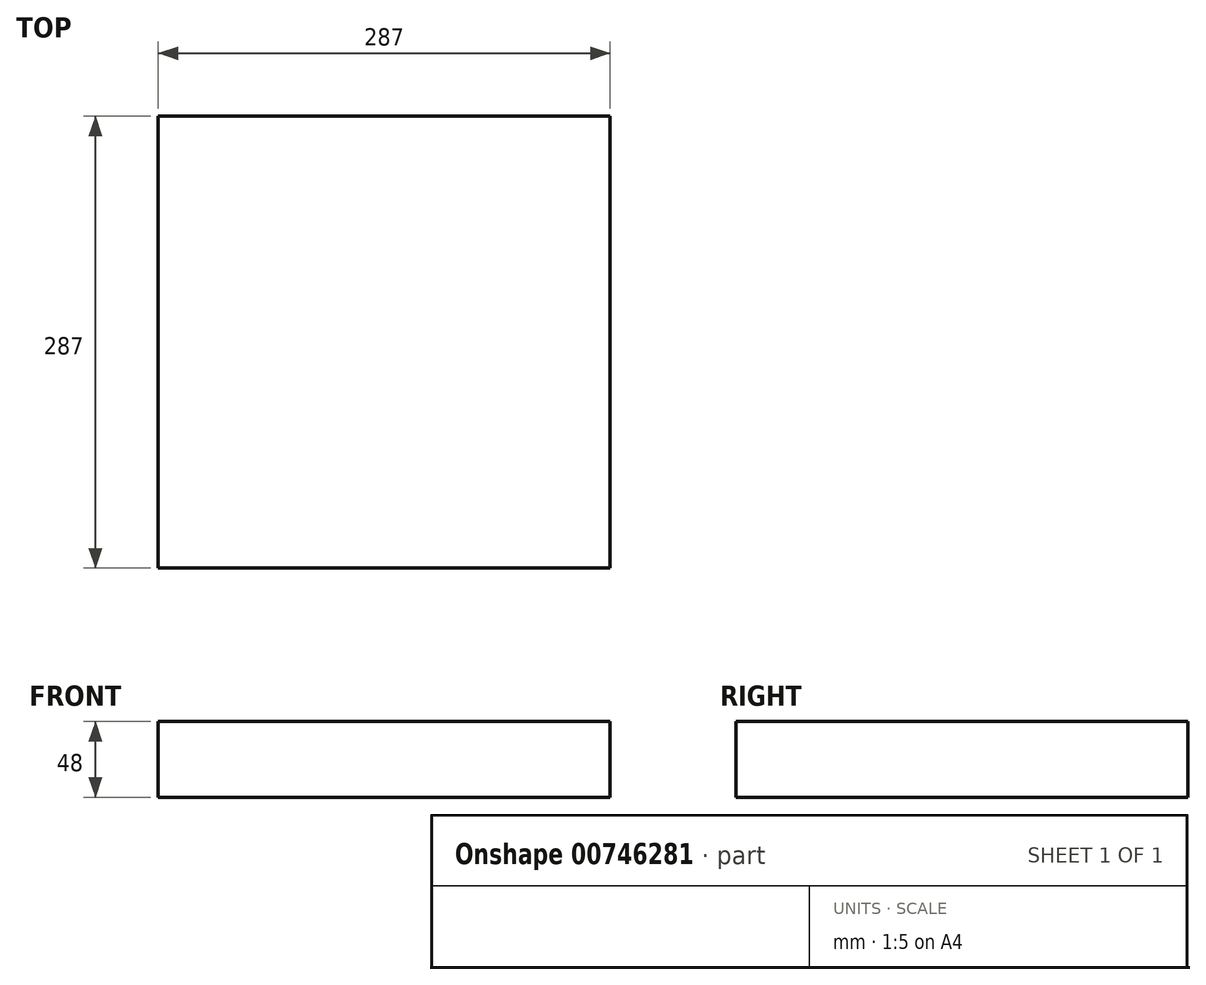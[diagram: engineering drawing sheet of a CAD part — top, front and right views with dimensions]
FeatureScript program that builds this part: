
annotation { "Feature Type Name" : "Feature", "Feature Type Description" : "" }
export const myFeature = defineFeature(function(context is Context, id is Id, definition is map)
    precondition{}
    {
        {
            var Q0;
            Q0=qCreatedBy(makeId("Top.planeOp"),FACE);
            var sketch = newSketch(context, id + "F0", { "sketchPlane" : qUnion([Q0])});
            skLineSegment(sketch, "E0.bottom", {"start": v(0, 0) * mm, "end": v(287, 0) * mm});
            skLineSegment(sketch, "E0.top", {"start": v(0, 287) * mm, "end": v(287, 287) * mm});
            skLineSegment(sketch, "E0.left", {"start": v(0, 0) * mm, "end": v(0, 287) * mm});
            skLineSegment(sketch, "E0.right", {"start": v(287, 0) * mm, "end": v(287, 287) * mm});
            skSolve(sketch);
        }
        {
            var Q0;
            Q0=makeQuery(id+"F0.imprint","IMPRINT",FACE,{"disambiguationData":[TD([[makeQuery(id+"F0.imprint","IMPRINT",EDGE,{"derivedFrom":sQuery(id+"F0.wireOp",EDGE,"E0.bottom")}),1.0]])]});
            extrude(context, id + "F1", {"entities" : qUnion([Q0]), "depth" : 48 * mm, "offsetDistance" : 25 * mm});
        }
    });
